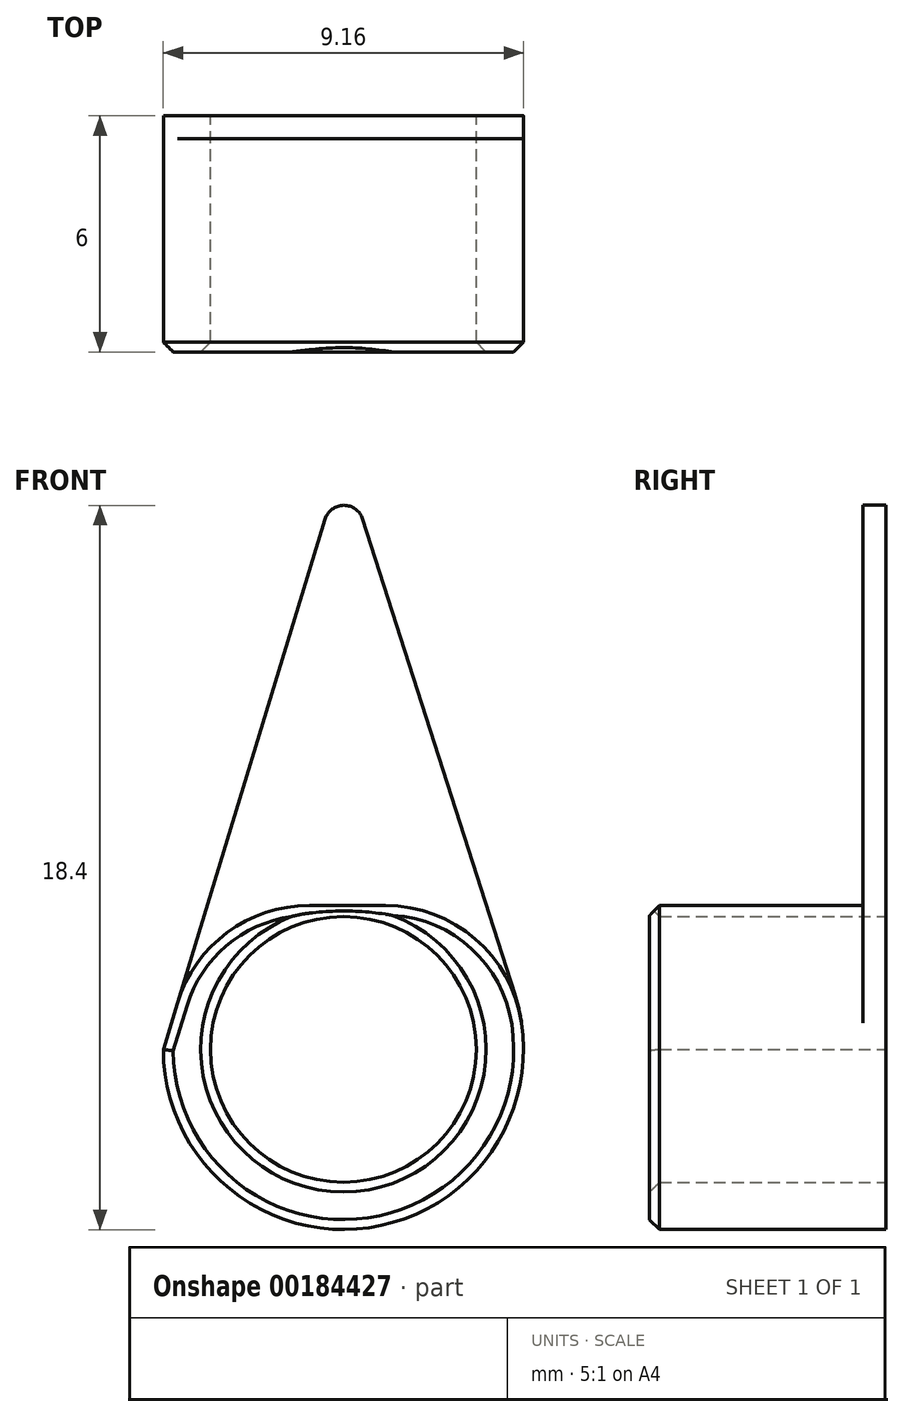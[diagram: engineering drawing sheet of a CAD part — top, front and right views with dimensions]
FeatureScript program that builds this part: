
annotation { "Feature Type Name" : "Feature", "Feature Type Description" : "" }
export const myFeature = defineFeature(function(context is Context, id is Id, definition is map)
    precondition{}
    {
        {
            var Q0;
            Q0=qCreatedBy(makeId("Front.planeOp"),FACE);
            var sketch = newSketch(context, id + "F0", { "sketchPlane" : qUnion([Q0])});
            skCircle(sketch, "E0", {"center": v(0, 0) * mm, "radius": 3.38 * mm});
            skArc(sketch, "E1", {"start": v(-4.58, 0) * mm, "mid": v(0.7, -4.52) * mm, "end": v(4.36, 1.4) * mm});
            skLineSegment(sketch, "E2", {"start": v(-4.58, 0) * mm, "end": v(0, 15) * mm});
            skLineSegment(sketch, "E3", {"start": v(0, 15) * mm, "end": v(4.36, 1.4) * mm});
            skPoint(sketch, "E4.orphan", {"position": v(4.8, 0) * mm});
            skSolve(sketch);
        }
        {
            var Q0;
            Q0=makeQuery(id+"F0.imprint","IMPRINT",FACE,{"disambiguationData":[TD([[makeQuery(id+"F0.imprint","IMPRINT",EDGE,{"derivedFrom":sQuery(id+"F0.wireOp",EDGE,"E0")}),-1.0]])]});
            extrude(context, id + "F1", {"entities" : qUnion([Q0]), "depth" : 6 * mm});
        }
        {
            var Q0;
            Q0=qCreatedBy(makeId("Right.planeOp"),FACE);
            var sketch = newSketch(context, id + "F2", { "sketchPlane" : qUnion([Q0])});
            skLineSegment(sketch, "E5.bottom", {"start": v(-8.97, 21.56) * mm, "end": v(-0.58, 21.56) * mm});
            skLineSegment(sketch, "E5.top", {"start": v(-8.97, 3.66) * mm, "end": v(-0.58, 3.66) * mm});
            skLineSegment(sketch, "E5.left", {"start": v(-8.97, 21.56) * mm, "end": v(-8.97, 3.66) * mm});
            skLineSegment(sketch, "E5.right", {"start": v(-0.58, 21.56) * mm, "end": v(-0.58, 3.66) * mm});
            skSolve(sketch);
        }
        {
            var Q0;
            Q0 = qSketchRegion(id + "F2", true);
            var Q1;
            Q1=makeQuery(id+"F2.imprint","IMPRINT",FACE,{"disambiguationData":[TD([[makeQuery(id+"F2.imprint","IMPRINT",EDGE,{"derivedFrom":sQuery(id+"F2.wireOp",EDGE,"E5.bottom")}),-1.0]])]});
            extrude(context, id + "F3", {"entities" : qUnion([Q0, Q1]), "operationType" : NewBodyOperationType.REMOVE, "endBound" : BoundingType.THROUGH_ALL, "oppositeDirection" : true, "depth" : 25 * mm, "hasSecondDirection" : true, "secondDirectionOppositeDirection" : false, "secondDirectionDepth" : 25 * mm});
        }
        {
            var Q0;
            Q0=makeQuery(id+"F3.boolean.opBoolean","INTERSECT",EDGE,{"derivedFrom":[makeQuery(id+"F1.opExtrude","SWEPT_FACE",FACE,{"disambiguationData":[OSD([sQuery(id+"F0.wireOp",EDGE,"E3")])]}),makeQuery(id+"F3.opExtrude","SWEPT_FACE",FACE,{"disambiguationData":[OSD([sQuery(id+"F2.wireOp",EDGE,"E5.top")])]})]});
            var Q1;
            Q1=makeQuery(id+"F3.boolean.opBoolean","INTERSECT",EDGE,{"derivedFrom":[makeQuery(id+"F1.opExtrude","SWEPT_FACE",FACE,{"disambiguationData":[OSD([sQuery(id+"F0.wireOp",EDGE,"E2")])]}),makeQuery(id+"F3.opExtrude","SWEPT_FACE",FACE,{"disambiguationData":[OSD([sQuery(id+"F2.wireOp",EDGE,"E5.top")])]})]});
            fillet(context, id + "F4", {"entities" : qUnion([Q0, Q1]), "radius" : 3.5 * mm, "tangentPropagation" : true, "allowEdgeOverflow" : false});
        }
        {
            var Q0;
            Q0=makeQuery(id+"F1.opExtrude","SWEPT_EDGE",EDGE,{"disambiguationData":[OSD([sQuery(id+"F0.wireOp",EDGE,"E2"),sQuery(id+"F0.wireOp",EDGE,"E3")])]});
            fillet(context, id + "F5", {"entities" : qUnion([Q0]), "radius" : 0.5 * mm, "tangentPropagation" : true, "allowEdgeOverflow" : false});
        }
        {
            var Q0;
            Q0=makeQuery(id+"F1.opExtrude","CAP_EDGE",EDGE,{"disambiguationData":[OSD([sQuery(id+"F0.wireOp",EDGE,"E0")])],"isStart":false});
            var Q1;
            Q1=makeQuery(id+"F1.opExtrude","CAP_FACE",FACE,{"disambiguationData":[OSD([sQuery(id+"F0.wireOp",EDGE,"E0"),sQuery(id+"F0.wireOp",EDGE,"E1"),sQuery(id+"F0.wireOp",EDGE,"E2"),sQuery(id+"F0.wireOp",EDGE,"E3")])],"isStart":false});
            chamfer(context, id + "F6", {"entities" : qUnion([Q0, Q1]), "width" : .25 * mm, "tangentPropagation" : true});
        }
    });
